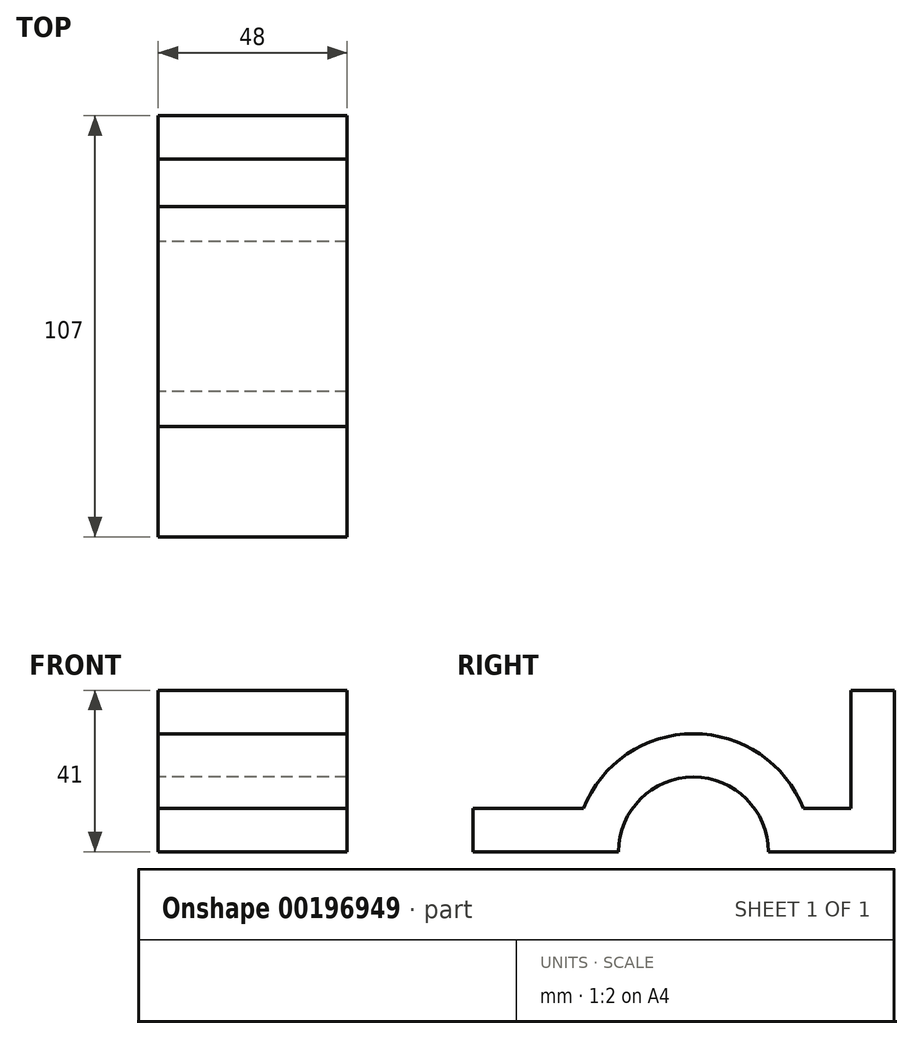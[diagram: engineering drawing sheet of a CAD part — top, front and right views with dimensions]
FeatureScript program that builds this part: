
annotation { "Feature Type Name" : "Feature", "Feature Type Description" : "" }
export const myFeature = defineFeature(function(context is Context, id is Id, definition is map)
    precondition{}
    {
        {
            var Q0;
            Q0=qCreatedBy(makeId("Right.planeOp"),FACE);
            var sketch = newSketch(context, id + "F0", { "sketchPlane" : qUnion([Q0])});
            skLineSegment(sketch, "E0", {"start": v(0.32, -17.88) * mm, "end": v(32.32, -17.88) * mm});
            skLineSegment(sketch, "E1", {"start": v(32.32, -17.88) * mm, "end": v(32.32, 23.12) * mm});
            skLineSegment(sketch, "E2", {"start": v(32.32, 23.12) * mm, "end": v(21.32, 23.12) * mm});
            skLineSegment(sketch, "E3", {"start": v(21.32, 23.12) * mm, "end": v(21.32, -6.88) * mm});
            skLineSegment(sketch, "E4", {"start": v(21.32, -6.88) * mm, "end": v(9.23, -6.88) * mm});
            skArc(sketch, "E5", {"start": v(0.32, -17.88) * mm, "mid": v(-18.68, 1.12) * mm, "end": v(-37.68, -17.88) * mm});
            skArc(sketch, "E6", {"start": v(9.23, -6.88) * mm, "mid": v(-18.68, 12.12) * mm, "end": v(-46.6, -6.88) * mm});
            skLineSegment(sketch, "E7", {"start": v(-37.68, -17.88) * mm, "end": v(-74.68, -17.88) * mm});
            skLineSegment(sketch, "E8", {"start": v(-74.68, -17.88) * mm, "end": v(-74.68, -6.88) * mm});
            skLineSegment(sketch, "E9", {"start": v(-74.68, -6.88) * mm, "end": v(-46.6, -6.88) * mm});
            skSolve(sketch);
        }
        {
            var Q0;
            Q0=makeQuery(id+"F0.imprint","IMPRINT",FACE,{"disambiguationData":[TD([[makeQuery(id+"F0.imprint","IMPRINT",EDGE,{"derivedFrom":sQuery(id+"F0.wireOp",EDGE,"E0")}),1.0]])]});
            extrude(context, id + "F1", {"entities" : qUnion([Q0]), "depth" : 48 * mm});
        }
    });
